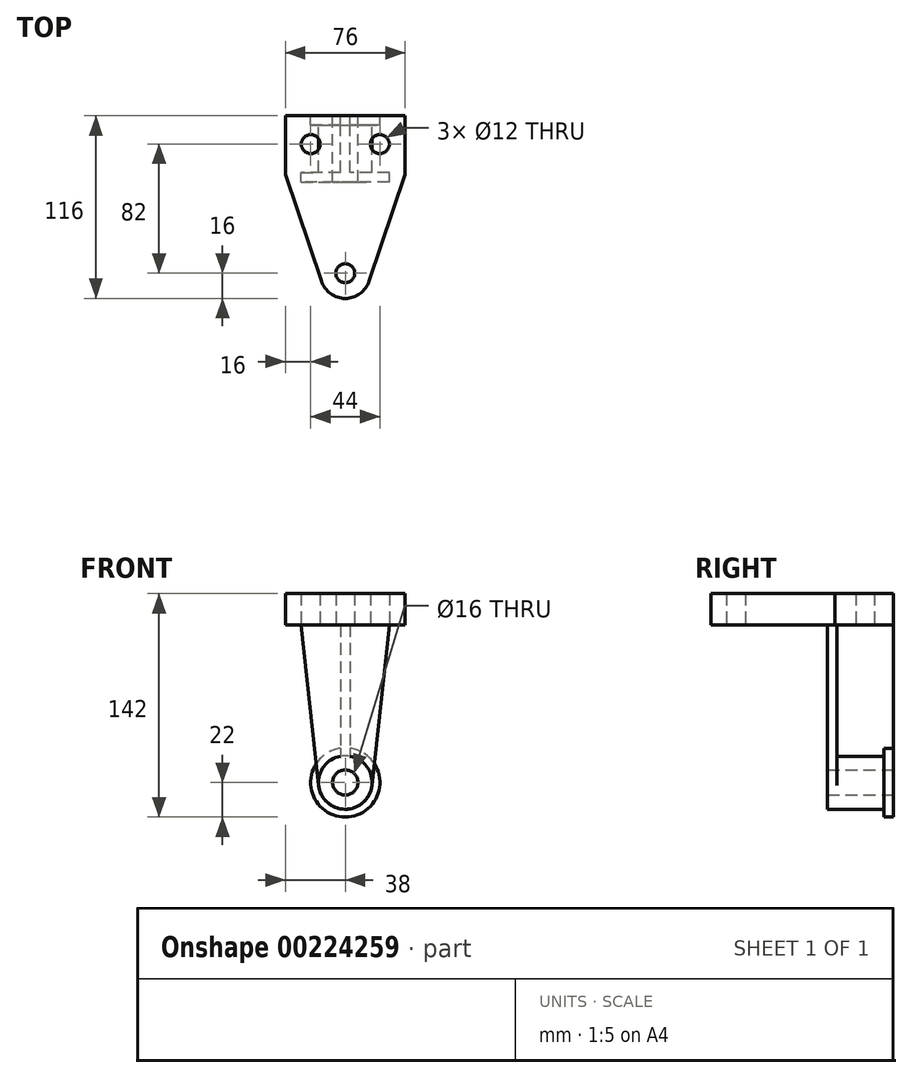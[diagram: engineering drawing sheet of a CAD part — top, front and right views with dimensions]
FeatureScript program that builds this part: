
annotation { "Feature Type Name" : "Feature", "Feature Type Description" : "" }
export const myFeature = defineFeature(function(context is Context, id is Id, definition is map)
    precondition{}
    {
        {
            var Q0;
            Q0=qCreatedBy(makeId("Front.planeOp"),FACE);
            var sketch = newSketch(context, id + "F0", { "sketchPlane" : qUnion([Q0])});
            skCircle(sketch, "E0", {"center": v(0, 0) * mm, "radius": 8 * mm});
            skCircle(sketch, "E1", {"center": v(0, 0) * mm, "radius": 22 * mm});
            skLineSegment(sketch, "E2", {"start": v(-38, 120) * mm, "end": v(38, 120) * mm});
            skLineSegment(sketch, "E3", {"start": v(38, 120) * mm, "end": v(38, 100) * mm});
            skLineSegment(sketch, "E4", {"start": v(38, 100) * mm, "end": v(-38, 100) * mm});
            skLineSegment(sketch, "E5", {"start": v(-38, 100) * mm, "end": v(-38, 120) * mm});
            skLineSegment(sketch, "E6", {"start": v(-3, 100) * mm, "end": v(-3, 21.8) * mm});
            skLineSegment(sketch, "E7", {"start": v(3, 100) * mm, "end": v(3, 21.8) * mm});
            skCircle(sketch, "E8", {"center": v(0, 0) * mm, "radius": 17 * mm});
            skLineSegment(sketch, "E9", {"start": v(-3, 21.8) * mm, "end": v(-3, 16.73) * mm});
            skLineSegment(sketch, "E10", {"start": v(3, 21.8) * mm, "end": v(3, 16.73) * mm});
            skSolve(sketch);
        }
        {
            var Q0;
            Q0=makeQuery(id+"F0.imprint","IMPRINT",FACE,{"disambiguationData":[TD([[makeQuery(id+"F0.imprint","IMPRINT",EDGE,{"derivedFrom":sQuery(id+"F0.wireOp",EDGE,"E0")}),-1.0]])]});
            extrude(context, id + "F1", {"entities" : qUnion([Q0]), "depth" : 40 * mm});
        }
        {
            var Q0;
            {var subQ0=sQuery(id+"F0.wireOp",EDGE,"E9");Q0=makeQuery(id+"F0.imprint","IMPRINT",FACE,{"disambiguationData":[TD([[makeQuery(id+"F0.imprint","IMPRINT",EDGE,{"derivedFrom":subQ0}),-1.0]])]});}
            extrude(context, id + "F2", {"entities" : qUnion([Q0]), "operationType" : NewBodyOperationType.ADD, "depth" : 6 * mm});
        }
        {
            var Q0;
            {var subQ0=sQuery(id+"F0.wireOp",EDGE,"E9");Q0=makeQuery(id+"F0.imprint","IMPRINT",FACE,{"disambiguationData":[TD([[makeQuery(id+"F0.imprint","IMPRINT",EDGE,{"derivedFrom":subQ0}),1.0]])]});}
            var Q1;
            {var subQ0=sQuery(id+"F0.wireOp",EDGE,"E6");Q1=makeQuery(id+"F0.imprint","IMPRINT",FACE,{"disambiguationData":[TD([[makeQuery(id+"F0.imprint","IMPRINT",EDGE,{"derivedFrom":subQ0}),1.0]])]});}
            extrude(context, id + "F3", {"entities" : qUnion([Q0, Q1]), "operationType" : NewBodyOperationType.ADD, "depth" : 40 * mm});
        }
        {
            var Q0;
            Q0=makeQuery(id+"F0.imprint","IMPRINT",FACE,{"disambiguationData":[TD([[makeQuery(id+"F0.imprint","IMPRINT",EDGE,{"derivedFrom":sQuery(id+"F0.wireOp",EDGE,"E2")}),-1.0]])]});
            extrude(context, id + "F4", {"entities" : qUnion([Q0]), "operationType" : NewBodyOperationType.ADD, "depth" : 116 * mm});
        }
        {
            var Q0;
            Q0=makeQuery(id+"F4.opExtrude","SWEPT_FACE",FACE,{"disambiguationData":[OSD([sQuery(id+"F0.wireOp",EDGE,"E4")])]});
            var sketch = newSketch(context, id + "F5", { "sketchPlane" : qUnion([Q0])});
            skCircle(sketch, "E11", {"center": v(-22, 18) * mm, "radius": 6 * mm});
            skCircle(sketch, "E12", {"center": v(22, 18) * mm, "radius": 6 * mm});
            skSolve(sketch);
        }
        {
            var Q0;
            Q0 = qSketchRegion(id + "F5", true);
            extrude(context, id + "F6", {"entities" : qUnion([Q0]), "operationType" : NewBodyOperationType.REMOVE, "oppositeDirection" : true, "depth" : 20 * mm});
        }
        {
            var Q0;
            Q0=makeQuery(id+"F0.imprint","IMPRINT",FACE,{"disambiguationData":[TD([[makeQuery(id+"F0.imprint","IMPRINT",EDGE,{"derivedFrom":sQuery(id+"F0.wireOp",EDGE,"E2")}),-1.0]])]});
            cPlane(context, id + "F7", {"entities" : qUnion([Q0]), "cplaneType" : CPlaneType.OFFSET, "offset" : 36 * mm, "width" : 150 * mm, "height" : 150 * mm});
        }
        {
            var Q0;
            Q0=qCreatedBy(id+"F7.planeOp",FACE);
            var sketch = newSketch(context, id + "F8", { "sketchPlane" : qUnion([Q0])});
            skCircle(sketch, "E13.0", {"center": v(0, 0) * mm, "radius": 17 * mm});
            skLineSegment(sketch, "E14.0", {"start": v(38, 100) * mm, "end": v(-38, 100) * mm});
            skLineSegment(sketch, "E15", {"start": v(-28, 100) * mm, "end": v(-16.9, -1.84) * mm});
            skLineSegment(sketch, "E16.0", {"start": v(-3, 100) * mm, "end": v(-3, 21.8) * mm});
            skLineSegment(sketch, "E17", {"start": v(0, -34.15) * mm, "end": v(0, 148.38) * mm});
            skLineSegment(sketch, "E18.MirrorCS", {"start": v(28, 100) * mm, "end": v(16.9, -1.84) * mm});
            skSolve(sketch);
        }
        {
            var Q0;
            Q0 = qSketchRegion(id + "F8", true);
            extrude(context, id + "F9", {"entities" : qUnion([Q0]), "operationType" : NewBodyOperationType.ADD, "depth" : 6 * mm});
        }
        {
            var Q0;
            Q0=makeQuery(id+"F4.opExtrude","SWEPT_FACE",FACE,{"disambiguationData":[OSD([sQuery(id+"F0.wireOp",EDGE,"E4")])]});
            var sketch = newSketch(context, id + "F10", { "sketchPlane" : qUnion([Q0])});
            skCircle(sketch, "E19", {"center": v(0, 100) * mm, "radius": 16 * mm});
            skCircle(sketch, "E20", {"center": v(0, 100) * mm, "radius": 6 * mm});
            skLineSegment(sketch, "E21", {"start": v(15.16, 105.11) * mm, "end": v(38, 37.37) * mm});
            skLineSegment(sketch, "E22", {"start": v(0, 100) * mm, "end": v(0, -44.21) * mm});
            skLineSegment(sketch, "E23.MirrorCS", {"start": v(-15.16, 105.11) * mm, "end": v(-38, 37.37) * mm});
            skSolve(sketch);
        }
        {
            var Q0;
            Q0=makeQuery(id+"F10.imprint","IMPRINT",FACE,{"disambiguationData":[TD([[makeQuery(id+"F10.imprint","IMPRINT",EDGE,{"derivedFrom":sQuery(id+"F10.wireOp",EDGE,"E20")}),1.0]])]});
            extrude(context, id + "F11", {"entities" : qUnion([Q0]), "operationType" : NewBodyOperationType.REMOVE, "oppositeDirection" : true, "depth" : 20 * mm});
        }
        {
            var Q0;
            {var subQ0=sQuery(id+"F10.wireOp",EDGE,"E21");Q0=makeQuery(id+"F10.imprint","IMPRINT",FACE,{"disambiguationData":[TD([[makeQuery(id+"F10.imprint","IMPRINT",EDGE,{"derivedFrom":subQ0}),1.0]])]});}
            var Q1;
            {var subQ0=sQuery(id+"F10.wireOp",EDGE,"E23.MirrorCS");Q1=makeQuery(id+"F10.imprint","IMPRINT",FACE,{"disambiguationData":[TD([[makeQuery(id+"F10.imprint","IMPRINT",EDGE,{"derivedFrom":subQ0}),-1.0]])]});}
            extrude(context, id + "F12", {"entities" : qUnion([Q0, Q1]), "operationType" : NewBodyOperationType.REMOVE, "oppositeDirection" : true, "depth" : 20 * mm});
        }
        {
            var Q0;
            {var subQ0=sQuery(id+"F0.wireOp",EDGE,"E0");Q0=makeQuery(id+"F9.boolean.opBoolean","SPLIT",FACE,{"disambiguationData":[TD([makeQuery(id+"F1.opExtrude","SWEPT_FACE",FACE,{"disambiguationData":[OSD([subQ0])]})])],"derivedFrom":makeQuery(id+"F9.opExtrude","CAP_FACE",FACE,{"disambiguationData":[OSD([sQuery(id+"F8.wireOp",EDGE,"E13.0"),sQuery(id+"F8.wireOp",EDGE,"E14.0"),sQuery(id+"F8.wireOp",EDGE,"E15"),sQuery(id+"F8.wireOp",EDGE,"E18.MirrorCS")])],"isStart":true})});}
            extrude(context, id + "F13", {"entities" : qUnion([Q0]), "operationType" : NewBodyOperationType.REMOVE, "endBound" : BoundingType.THROUGH_ALL, "oppositeDirection" : true, "depth" : 25 * mm});
        }
    });
